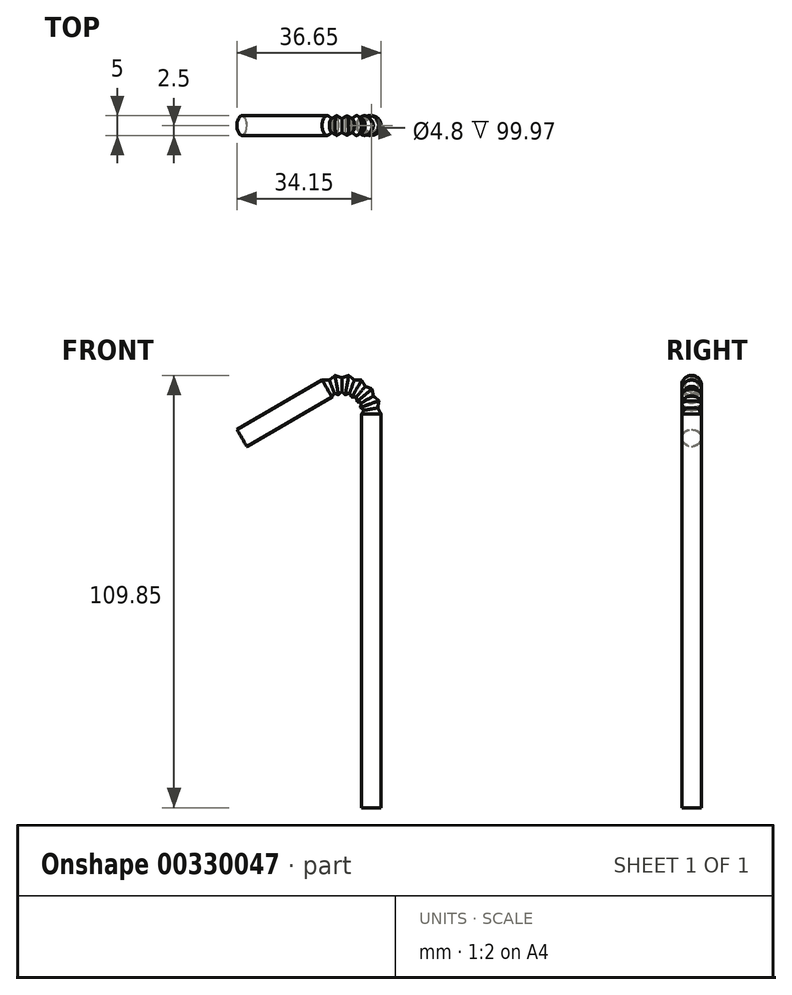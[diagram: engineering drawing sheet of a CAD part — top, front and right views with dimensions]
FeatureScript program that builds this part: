
annotation { "Feature Type Name" : "Feature", "Feature Type Description" : "" }
export const myFeature = defineFeature(function(context is Context, id is Id, definition is map)
    precondition{}
    {
        {
            var Q0;
            Q0=qCreatedBy(makeId("Top.planeOp"),FACE);
            cPlane(context, id + "F0", {"entities" : qUnion([Q0]), "cplaneType" : CPlaneType.OFFSET, "offset" : 50 * mm, "oppositeDirection" : true, "width" : 150 * mm, "height" : 150 * mm});
        }
        {
            var Q0;
            Q0=qCreatedBy(id+"F0.planeOp",FACE);
            cPlane(context, id + "F1", {"entities" : qUnion([Q0]), "cplaneType" : CPlaneType.OFFSET, "offset" : 100 * mm, "width" : 150 * mm, "height" : 150 * mm});
        }
        {
            var Q0;
            Q0=qCreatedBy(id+"F0.planeOp",FACE);
            var sketch = newSketch(context, id + "F2", { "sketchPlane" : qUnion([Q0])});
            skCircle(sketch, "E0", {"center": v(0, 0) * mm, "radius": 2.5 * mm});
            skSolve(sketch);
        }
        {
            var Q0;
            Q0=qCreatedBy(id+"F1.planeOp",FACE);
            var sketch = newSketch(context, id + "F3", { "sketchPlane" : qUnion([Q0])});
            skCircle(sketch, "E1", {"center": v(0, 0) * mm, "radius": 2.5 * mm});
            skSolve(sketch);
        }
        {
            var Q0;
            Q0=makeQuery(id+"F2.imprint","IMPRINT",FACE,{"disambiguationData":[TD([[makeQuery(id+"F2.imprint","IMPRINT",EDGE,{"derivedFrom":sQuery(id+"F2.wireOp",EDGE,"E0")}),1.0]])]});
            var Q1;
            Q1=makeQuery(id+"F3.imprint","IMPRINT",FACE,{"disambiguationData":[TD([[makeQuery(id+"F3.imprint","IMPRINT",EDGE,{"derivedFrom":sQuery(id+"F3.wireOp",EDGE,"E1")}),1.0]])]});
            loft(context, id + "F4", {"sheetProfilesArray" : [{ "sheetProfileEntities" : qUnion([Q0]) }, { "sheetProfileEntities" : qUnion([Q1]) }]});
        }
        {
            var Q0;
            Q0=qCreatedBy(id+"F1.planeOp",FACE);
            var sketch = newSketch(context, id + "F5", { "sketchPlane" : qUnion([Q0])});
            skLineSegment(sketch, "E2", {"start": v(-7.5, 11.95) * mm, "end": v(-7.5, -17.6) * mm, "construction": true});
            skSolve(sketch);
        }
        {
            var Q0;
            Q0=sQuery(id+"F5.wireOp",EDGE,"E2");
            var Q1;
            Q1=qCreatedBy(id+"F1.planeOp",FACE);
            cPlane(context, id + "F6", {"entities" : qUnion([Q0, Q1]), "cplaneType" : CPlaneType.LINE_ANGLE, "offset" : 25 * mm, "angle" : 10 * degree, "width" : 150 * mm, "height" : 150 * mm});
        }
        {
            var Q0;
            Q0=qCreatedBy(id+"F1.planeOp",FACE);
            var Q1;
            Q1=sQuery(id+"F5.wireOp",EDGE,"E2");
            cPlane(context, id + "F7", {"entities" : qUnion([Q0, Q1]), "cplaneType" : CPlaneType.LINE_ANGLE, "offset" : 25 * mm, "angle" : 20 * degree, "width" : 150 * mm, "height" : 150 * mm});
        }
        {
            var Q0;
            Q0=sQuery(id+"F5.wireOp",EDGE,"E2");
            var Q1;
            Q1=qCreatedBy(id+"F1.planeOp",FACE);
            cPlane(context, id + "F8", {"entities" : qUnion([Q0, Q1]), "cplaneType" : CPlaneType.LINE_ANGLE, "offset" : 25 * mm, "angle" : 30 * degree, "width" : 150 * mm, "height" : 150 * mm});
        }
        {
            var Q0;
            Q0=sQuery(id+"F5.wireOp",EDGE,"E2");
            var Q1;
            Q1=qCreatedBy(id+"F1.planeOp",FACE);
            cPlane(context, id + "F9", {"entities" : qUnion([Q0, Q1]), "cplaneType" : CPlaneType.LINE_ANGLE, "offset" : 25 * mm, "angle" : 40 * degree, "width" : 150 * mm, "height" : 150 * mm});
        }
        {
            var Q0;
            Q0=sQuery(id+"F5.wireOp",EDGE,"E2");
            var Q1;
            Q1=qCreatedBy(id+"F1.planeOp",FACE);
            cPlane(context, id + "F10", {"entities" : qUnion([Q0, Q1]), "cplaneType" : CPlaneType.LINE_ANGLE, "offset" : 25 * mm, "angle" : 50 * degree, "width" : 150 * mm, "height" : 150 * mm});
        }
        {
            var Q0;
            Q0=sQuery(id+"F5.wireOp",EDGE,"E2");
            var Q1;
            Q1=qCreatedBy(id+"F1.planeOp",FACE);
            cPlane(context, id + "F11", {"entities" : qUnion([Q0, Q1]), "cplaneType" : CPlaneType.LINE_ANGLE, "offset" : 25 * mm, "angle" : 60 * degree, "width" : 150 * mm, "height" : 150 * mm});
        }
        {
            var Q0;
            Q0=sQuery(id+"F5.wireOp",EDGE,"E2");
            var Q1;
            Q1=qCreatedBy(id+"F1.planeOp",FACE);
            cPlane(context, id + "F12", {"entities" : qUnion([Q0, Q1]), "cplaneType" : CPlaneType.LINE_ANGLE, "offset" : 25 * mm, "angle" : 70 * degree, "width" : 150 * mm, "height" : 150 * mm});
        }
        {
            var Q0;
            Q0=sQuery(id+"F5.wireOp",EDGE,"E2");
            var Q1;
            Q1=qCreatedBy(id+"F1.planeOp",FACE);
            cPlane(context, id + "F13", {"entities" : qUnion([Q0, Q1]), "cplaneType" : CPlaneType.LINE_ANGLE, "offset" : 25 * mm, "angle" : 80 * degree, "width" : 150 * mm, "height" : 150 * mm});
        }
        {
            var Q0;
            Q0=sQuery(id+"F5.wireOp",EDGE,"E2");
            var Q1;
            Q1=qCreatedBy(id+"F1.planeOp",FACE);
            cPlane(context, id + "F14", {"entities" : qUnion([Q0, Q1]), "cplaneType" : CPlaneType.LINE_ANGLE, "offset" : 25 * mm, "angle" : 90 * degree, "width" : 150 * mm, "height" : 150 * mm});
        }
        {
            var Q0;
            Q0=sQuery(id+"F5.wireOp",EDGE,"E2");
            cPlane(context, id + "F15", {"entities" : qUnion([Q0]), "cplaneType" : CPlaneType.LINE_ANGLE, "offset" : 25 * mm, "angle" : 100 * degree, "width" : 150 * mm, "height" : 150 * mm});
        }
        {
            var Q0;
            Q0=sQuery(id+"F5.wireOp",EDGE,"E2");
            var Q1;
            Q1=qCreatedBy(id+"F1.planeOp",FACE);
            cPlane(context, id + "F16", {"entities" : qUnion([Q0, Q1]), "cplaneType" : CPlaneType.LINE_ANGLE, "offset" : 25 * mm, "angle" : 110 * degree, "width" : 150 * mm, "height" : 150 * mm});
        }
        {
            var Q0;
            Q0=sQuery(id+"F5.wireOp",EDGE,"E2");
            var Q1;
            Q1=qCreatedBy(id+"F1.planeOp",FACE);
            cPlane(context, id + "F17", {"entities" : qUnion([Q0, Q1]), "cplaneType" : CPlaneType.LINE_ANGLE, "offset" : 25 * mm, "angle" : 120 * degree, "width" : 150 * mm, "height" : 150 * mm});
        }
        {
            var Q0;
            Q0=makeQuery(id+"F4.opLoft","CAP_FACE",FACE,{"disambiguationData":[OSD([makeQuery(id+"F3.imprint","IMPRINT",FACE,{"disambiguationData":[TD([[makeQuery(id+"F3.imprint","IMPRINT",EDGE,{"derivedFrom":sQuery(id+"F3.wireOp",EDGE,"E1")}),1.0]])]})])],"isStart":true});
            var sketch = newSketch(context, id + "F18", { "sketchPlane" : qUnion([Q0])});
            skPoint(sketch, "E3", {"position": v(0, 0) * mm});
            skLineSegment(sketch, "E4", {"start": v(-5.52, 0) * mm, "end": v(6.44, 0) * mm, "construction": true});
            skSolve(sketch);
        }
        {
            var Q0;
            Q0=qCreatedBy(id+"F6.planeOp",FACE);
            var sketch = newSketch(context, id + "F19", { "sketchPlane" : qUnion([Q0])});
            skCircle(sketch, "E5", {"center": v(8.8, 0) * mm, "radius": 1.75 * mm});
            skSolve(sketch);
        }
        {
            var Q0;
            Q0=qCreatedBy(id+"F7.planeOp",FACE);
            var sketch = newSketch(context, id + "F20", { "sketchPlane" : qUnion([Q0])});
            skCircle(sketch, "E6", {"center": v(17.55, 0) * mm, "radius": 2.5 * mm});
            skSolve(sketch);
        }
        {
            var Q0;
            Q0=qCreatedBy(id+"F8.planeOp",FACE);
            var sketch = newSketch(context, id + "F21", { "sketchPlane" : qUnion([Q0])});
            skCircle(sketch, "E7", {"center": v(26, 0) * mm, "radius": 1.75 * mm});
            skSolve(sketch);
        }
        {
            var Q0;
            Q0=qCreatedBy(id+"F9.planeOp",FACE);
            var sketch = newSketch(context, id + "F22", { "sketchPlane" : qUnion([Q0])});
            skCircle(sketch, "E8", {"center": v(33.9, 0) * mm, "radius": 2.5 * mm});
            skSolve(sketch);
        }
        {
            var Q1;
            Q1=makeQuery(id+"F18.imprint","IMPRINT",FACE,{"disambiguationData":[TD([[makeQuery(id+"F18.imprint","IMPRINT",EDGE,{"derivedFrom":makeQuery(id+"F4.opLoft","MID_CAP_EDGE",EDGE,{"disambiguationData":[OSD([sQuery(id+"F2.wireOp",EDGE,"E0"),sQuery(id+"F3.wireOp",EDGE,"E1")])],"capPos":1.0})}),1.0]])]});
            var Q2;
            Q2=makeQuery(id+"F19.imprint","IMPRINT",FACE,{"disambiguationData":[TD([[makeQuery(id+"F19.imprint","IMPRINT",EDGE,{"derivedFrom":sQuery(id+"F19.wireOp",EDGE,"E5")}),1.0]])]});
            loft(context, id + "F23", {"operationType" : NewBodyOperationType.ADD, "sheetProfilesArray" : [{ "sheetProfileEntities" : qUnion([Q1]) }, { "sheetProfileEntities" : qUnion([Q2]) }]});
        }
        {
            var Q0;
            Q0=qCreatedBy(id+"F10.planeOp",FACE);
            var sketch = newSketch(context, id + "F24", { "sketchPlane" : qUnion([Q0])});
            skCircle(sketch, "E9", {"center": v(0, 40.98) * mm, "radius": 1.75 * mm});
            skSolve(sketch);
        }
        {
            var Q0;
            Q0=qCreatedBy(id+"F11.planeOp",FACE);
            var sketch = newSketch(context, id + "F25", { "sketchPlane" : qUnion([Q0])});
            skCircle(sketch, "E10", {"center": v(0, 47.05) * mm, "radius": 2.5 * mm});
            skSolve(sketch);
        }
        {
            var Q0;
            Q0=qCreatedBy(id+"F12.planeOp",FACE);
            var sketch = newSketch(context, id + "F26", { "sketchPlane" : qUnion([Q0])});
            skCircle(sketch, "E11", {"center": v(0, 51.92) * mm, "radius": 1.75 * mm});
            skSolve(sketch);
        }
        {
            var Q1;
            Q1=makeQuery(id+"F23.opLoft","CAP_FACE",FACE,{"disambiguationData":[OSD([makeQuery(id+"F19.imprint","IMPRINT",FACE,{"disambiguationData":[TD([[makeQuery(id+"F19.imprint","IMPRINT",EDGE,{"derivedFrom":sQuery(id+"F19.wireOp",EDGE,"E5")}),1.0]])]})])],"isStart":true});
            var Q2;
            Q2=makeQuery(id+"F20.imprint","IMPRINT",FACE,{"disambiguationData":[TD([[makeQuery(id+"F20.imprint","IMPRINT",EDGE,{"derivedFrom":sQuery(id+"F20.wireOp",EDGE,"E6")}),1.0]])]});
            loft(context, id + "F27", {"operationType" : NewBodyOperationType.ADD, "sheetProfilesArray" : [{ "sheetProfileEntities" : qUnion([Q1]) }, { "sheetProfileEntities" : qUnion([Q2]) }]});
        }
        {
            var Q1;
            Q1=makeQuery(id+"F27.opLoft","CAP_FACE",FACE,{"disambiguationData":[OSD([makeQuery(id+"F20.imprint","IMPRINT",FACE,{"disambiguationData":[TD([[makeQuery(id+"F20.imprint","IMPRINT",EDGE,{"derivedFrom":sQuery(id+"F20.wireOp",EDGE,"E6")}),1.0]])]})])],"isStart":true});
            var Q2;
            Q2=makeQuery(id+"F21.imprint","IMPRINT",FACE,{"disambiguationData":[TD([[makeQuery(id+"F21.imprint","IMPRINT",EDGE,{"derivedFrom":sQuery(id+"F21.wireOp",EDGE,"E7")}),1.0]])]});
            loft(context, id + "F28", {"operationType" : NewBodyOperationType.ADD, "sheetProfilesArray" : [{ "sheetProfileEntities" : qUnion([Q1]) }, { "sheetProfileEntities" : qUnion([Q2]) }]});
        }
        {
            var Q1;
            Q1=makeQuery(id+"F28.opLoft","CAP_FACE",FACE,{"disambiguationData":[OSD([makeQuery(id+"F21.imprint","IMPRINT",FACE,{"disambiguationData":[TD([[makeQuery(id+"F21.imprint","IMPRINT",EDGE,{"derivedFrom":sQuery(id+"F21.wireOp",EDGE,"E7")}),1.0]])]})])],"isStart":true});
            var Q2;
            Q2=makeQuery(id+"F22.imprint","IMPRINT",FACE,{"disambiguationData":[TD([[makeQuery(id+"F22.imprint","IMPRINT",EDGE,{"derivedFrom":sQuery(id+"F22.wireOp",EDGE,"E8")}),1.0]])]});
            loft(context, id + "F29", {"operationType" : NewBodyOperationType.ADD, "sheetProfilesArray" : [{ "sheetProfileEntities" : qUnion([Q1]) }, { "sheetProfileEntities" : qUnion([Q2]) }]});
        }
        {
            var Q1;
            Q1=makeQuery(id+"F29.opLoft","CAP_FACE",FACE,{"disambiguationData":[OSD([makeQuery(id+"F22.imprint","IMPRINT",FACE,{"disambiguationData":[TD([[makeQuery(id+"F22.imprint","IMPRINT",EDGE,{"derivedFrom":sQuery(id+"F22.wireOp",EDGE,"E8")}),1.0]])]})])],"isStart":true});
            var Q2;
            Q2=makeQuery(id+"F24.imprint","IMPRINT",FACE,{"disambiguationData":[TD([[makeQuery(id+"F24.imprint","IMPRINT",EDGE,{"derivedFrom":sQuery(id+"F24.wireOp",EDGE,"E9")}),1.0]])]});
            loft(context, id + "F30", {"operationType" : NewBodyOperationType.ADD, "sheetProfilesArray" : [{ "sheetProfileEntities" : qUnion([Q1]) }, { "sheetProfileEntities" : qUnion([Q2]) }]});
        }
        {
            var Q1;
            Q1=makeQuery(id+"F30.opLoft","CAP_FACE",FACE,{"disambiguationData":[OSD([makeQuery(id+"F24.imprint","IMPRINT",FACE,{"disambiguationData":[TD([[makeQuery(id+"F24.imprint","IMPRINT",EDGE,{"derivedFrom":sQuery(id+"F24.wireOp",EDGE,"E9")}),1.0]])]})])],"isStart":true});
            var Q2;
            Q2=makeQuery(id+"F25.imprint","IMPRINT",FACE,{"disambiguationData":[TD([[makeQuery(id+"F25.imprint","IMPRINT",EDGE,{"derivedFrom":sQuery(id+"F25.wireOp",EDGE,"E10")}),1.0]])]});
            loft(context, id + "F31", {"operationType" : NewBodyOperationType.ADD, "sheetProfilesArray" : [{ "sheetProfileEntities" : qUnion([Q1]) }, { "sheetProfileEntities" : qUnion([Q2]) }]});
        }
        {
            var Q1;
            Q1=makeQuery(id+"F31.opLoft","CAP_FACE",FACE,{"disambiguationData":[OSD([makeQuery(id+"F25.imprint","IMPRINT",FACE,{"disambiguationData":[TD([[makeQuery(id+"F25.imprint","IMPRINT",EDGE,{"derivedFrom":sQuery(id+"F25.wireOp",EDGE,"E10")}),1.0]])]})])],"isStart":true});
            var Q2;
            Q2=makeQuery(id+"F26.imprint","IMPRINT",FACE,{"disambiguationData":[TD([[makeQuery(id+"F26.imprint","IMPRINT",EDGE,{"derivedFrom":sQuery(id+"F26.wireOp",EDGE,"E11")}),1.0]])]});
            loft(context, id + "F32", {"operationType" : NewBodyOperationType.ADD, "sheetProfilesArray" : [{ "sheetProfileEntities" : qUnion([Q1]) }, { "sheetProfileEntities" : qUnion([Q2]) }]});
        }
        {
            var Q0;
            Q0=qCreatedBy(id+"F13.planeOp",FACE);
            var sketch = newSketch(context, id + "F33", { "sketchPlane" : qUnion([Q0])});
            skCircle(sketch, "E12", {"center": v(0, 55.44) * mm, "radius": 2.5 * mm});
            skSolve(sketch);
        }
        {
            var Q1;
            Q1=makeQuery(id+"F32.opLoft","CAP_FACE",FACE,{"disambiguationData":[OSD([makeQuery(id+"F26.imprint","IMPRINT",FACE,{"disambiguationData":[TD([[makeQuery(id+"F26.imprint","IMPRINT",EDGE,{"derivedFrom":sQuery(id+"F26.wireOp",EDGE,"E11")}),1.0]])]})])],"isStart":true});
            var Q2;
            Q2=makeQuery(id+"F33.imprint","IMPRINT",FACE,{"disambiguationData":[TD([[makeQuery(id+"F33.imprint","IMPRINT",EDGE,{"derivedFrom":sQuery(id+"F33.wireOp",EDGE,"E12")}),1.0]])]});
            loft(context, id + "F34", {"operationType" : NewBodyOperationType.ADD, "sheetProfilesArray" : [{ "sheetProfileEntities" : qUnion([Q1]) }, { "sheetProfileEntities" : qUnion([Q2]) }]});
        }
        {
            var Q0;
            Q0=qCreatedBy(id+"F14.planeOp",FACE);
            var sketch = newSketch(context, id + "F35", { "sketchPlane" : qUnion([Q0])});
            skCircle(sketch, "E13", {"center": v(0, 57.5) * mm, "radius": 1.75 * mm});
            skLineSegment(sketch, "E14", {"start": v(0, 0) * mm, "end": v(0, 65.17) * mm, "construction": true});
            skSolve(sketch);
        }
        {
            var Q1;
            Q1=makeQuery(id+"F34.opLoft","CAP_FACE",FACE,{"disambiguationData":[OSD([makeQuery(id+"F33.imprint","IMPRINT",FACE,{"disambiguationData":[TD([[makeQuery(id+"F33.imprint","IMPRINT",EDGE,{"derivedFrom":sQuery(id+"F33.wireOp",EDGE,"E12")}),1.0]])]})])],"isStart":true});
            var Q2;
            Q2=makeQuery(id+"F35.imprint","IMPRINT",FACE,{"disambiguationData":[TD([[makeQuery(id+"F35.imprint","IMPRINT",EDGE,{"derivedFrom":sQuery(id+"F35.wireOp",EDGE,"E13")}),1.0]])]});
            loft(context, id + "F36", {"operationType" : NewBodyOperationType.ADD, "sheetProfilesArray" : [{ "sheetProfileEntities" : qUnion([Q1]) }, { "sheetProfileEntities" : qUnion([Q2]) }]});
        }
        {
            var Q0;
            Q0=qCreatedBy(id+"F15.planeOp",FACE);
            var sketch = newSketch(context, id + "F37", { "sketchPlane" : qUnion([Q0])});
            skCircle(sketch, "E15", {"center": v(0, 58.04) * mm, "radius": 2.5 * mm});
            skSolve(sketch);
        }
        {
            var Q1;
            Q1=makeQuery(id+"F35.imprint","IMPRINT",FACE,{"disambiguationData":[TD([[makeQuery(id+"F35.imprint","IMPRINT",EDGE,{"derivedFrom":sQuery(id+"F35.wireOp",EDGE,"E13")}),1.0]])]});
            var Q2;
            Q2=makeQuery(id+"F37.imprint","IMPRINT",FACE,{"disambiguationData":[TD([[makeQuery(id+"F37.imprint","IMPRINT",EDGE,{"derivedFrom":sQuery(id+"F37.wireOp",EDGE,"E15")}),1.0]])]});
            loft(context, id + "F38", {"operationType" : NewBodyOperationType.ADD, "sheetProfilesArray" : [{ "sheetProfileEntities" : qUnion([Q1]) }, { "sheetProfileEntities" : qUnion([Q2]) }]});
        }
        {
            var Q0;
            Q0=qCreatedBy(id+"F16.planeOp",FACE);
            var sketch = newSketch(context, id + "F39", { "sketchPlane" : qUnion([Q0])});
            skCircle(sketch, "E16", {"center": v(0, 57.05) * mm, "radius": 1.75 * mm});
            skSolve(sketch);
        }
        {
            var Q1;
            Q1=makeQuery(id+"F38.opLoft","CAP_FACE",FACE,{"disambiguationData":[OSD([makeQuery(id+"F37.imprint","IMPRINT",FACE,{"disambiguationData":[TD([[makeQuery(id+"F37.imprint","IMPRINT",EDGE,{"derivedFrom":sQuery(id+"F37.wireOp",EDGE,"E15")}),1.0]])]})])],"isStart":true});
            var Q2;
            Q2=makeQuery(id+"F39.imprint","IMPRINT",FACE,{"disambiguationData":[TD([[makeQuery(id+"F39.imprint","IMPRINT",EDGE,{"derivedFrom":sQuery(id+"F39.wireOp",EDGE,"E16")}),1.0]])]});
            loft(context, id + "F40", {"operationType" : NewBodyOperationType.ADD, "sheetProfilesArray" : [{ "sheetProfileEntities" : qUnion([Q1]) }, { "sheetProfileEntities" : qUnion([Q2]) }]});
        }
        {
            var Q0;
            Q0=qCreatedBy(id+"F17.planeOp",FACE);
            var sketch = newSketch(context, id + "F41", { "sketchPlane" : qUnion([Q0])});
            skCircle(sketch, "E17", {"center": v(0, 54.55) * mm, "radius": 2.5 * mm});
            skSolve(sketch);
        }
        {
            var Q1;
            Q1=makeQuery(id+"F40.opLoft","CAP_FACE",FACE,{"disambiguationData":[OSD([makeQuery(id+"F39.imprint","IMPRINT",FACE,{"disambiguationData":[TD([[makeQuery(id+"F39.imprint","IMPRINT",EDGE,{"derivedFrom":sQuery(id+"F39.wireOp",EDGE,"E16")}),1.0]])]})])],"isStart":true});
            var Q2;
            Q2=makeQuery(id+"F41.imprint","IMPRINT",FACE,{"disambiguationData":[TD([[makeQuery(id+"F41.imprint","IMPRINT",EDGE,{"derivedFrom":sQuery(id+"F41.wireOp",EDGE,"E17")}),1.0]])]});
            loft(context, id + "F42", {"operationType" : NewBodyOperationType.ADD, "sheetProfilesArray" : [{ "sheetProfileEntities" : qUnion([Q1]) }, { "sheetProfileEntities" : qUnion([Q2]) }]});
        }
        {
            var Q0;
            Q0=qCreatedBy(id+"F17.planeOp",FACE);
            cPlane(context, id + "F43", {"entities" : qUnion([Q0]), "cplaneType" : CPlaneType.OFFSET, "offset" : 25 * mm, "oppositeDirection" : true, "width" : 150 * mm, "height" : 150 * mm});
        }
        {
            var Q0;
            Q0=qCreatedBy(id+"F43.planeOp",FACE);
            var sketch = newSketch(context, id + "F44", { "sketchPlane" : qUnion([Q0])});
            skCircle(sketch, "E18", {"center": v(0, 562.03) * mm, "radius": 25 * mm});
            skCircle(sketch, "E19", {"center": v(0, 54.55) * mm, "radius": 2.5 * mm});
            skSolve(sketch);
        }
        {
            var Q1;
            Q1=makeQuery(id+"F42.opLoft","CAP_FACE",FACE,{"disambiguationData":[OSD([makeQuery(id+"F41.imprint","IMPRINT",FACE,{"disambiguationData":[TD([[makeQuery(id+"F41.imprint","IMPRINT",EDGE,{"derivedFrom":sQuery(id+"F41.wireOp",EDGE,"E17")}),1.0]])]})])],"isStart":true});
            var Q2;
            Q2=makeQuery(id+"F44.imprint","IMPRINT",FACE,{"disambiguationData":[TD([[makeQuery(id+"F44.imprint","IMPRINT",EDGE,{"derivedFrom":sQuery(id+"F44.wireOp",EDGE,"E19")}),1.0]])]});
            loft(context, id + "F45", {"operationType" : NewBodyOperationType.ADD, "sheetProfilesArray" : [{ "sheetProfileEntities" : qUnion([Q1]) }, { "sheetProfileEntities" : qUnion([Q2]) }]});
        }
        {
            var Q0;
            Q0=makeQuery(id+"F45.opLoft","CAP_FACE",FACE,{"disambiguationData":[OSD([makeQuery(id+"F44.imprint","IMPRINT",FACE,{"disambiguationData":[TD([[makeQuery(id+"F44.imprint","IMPRINT",EDGE,{"derivedFrom":sQuery(id+"F44.wireOp",EDGE,"E19")}),1.0]])]})])],"isStart":true});
            shell(context, id + "F46", {"entities" : qUnion([Q0]), "thickness" : 0.1 * mm});
        }
        {
            var Q0;
            Q0=makeQuery(id+"F4.opLoft","CAP_FACE",FACE,{"disambiguationData":[OSD([makeQuery(id+"F2.imprint","IMPRINT",FACE,{"disambiguationData":[TD([[makeQuery(id+"F2.imprint","IMPRINT",EDGE,{"derivedFrom":sQuery(id+"F2.wireOp",EDGE,"E0")}),1.0]])]})])],"isStart":true});
            var sketch = newSketch(context, id + "F47", { "sketchPlane" : qUnion([Q0])});
            skCircle(sketch, "E20", {"center": v(0, 0) * mm, "radius": 2.4 * mm});
            skSolve(sketch);
        }
        {
            var Q0;
            Q0=makeQuery(id+"F47.imprint","IMPRINT",FACE,{"disambiguationData":[TD([[makeQuery(id+"F47.imprint","IMPRINT",EDGE,{"derivedFrom":sQuery(id+"F47.wireOp",EDGE,"E20")}),1.0]])]});
            extrude(context, id + "F48", {"entities" : qUnion([Q0]), "operationType" : NewBodyOperationType.REMOVE, "oppositeDirection" : true, "depth" : 25 * mm});
        }
    });
